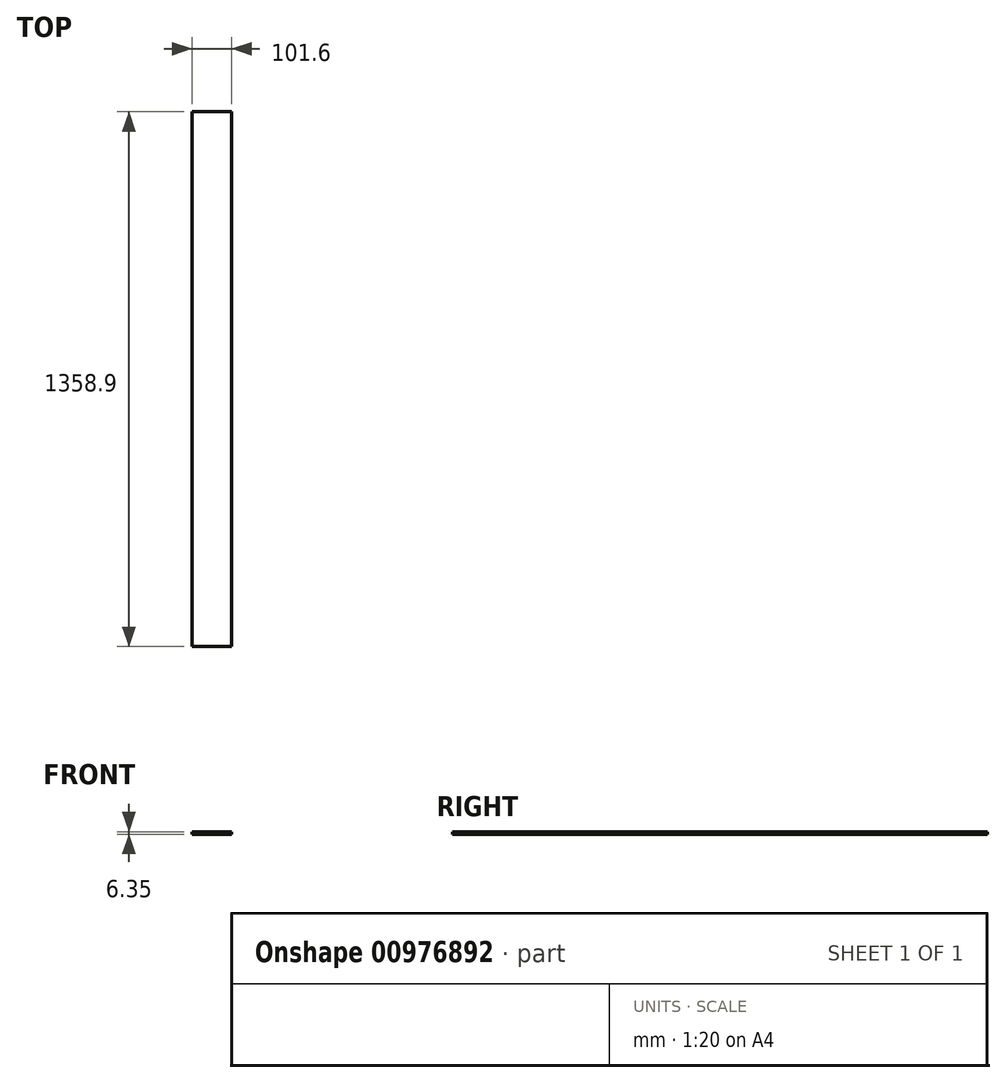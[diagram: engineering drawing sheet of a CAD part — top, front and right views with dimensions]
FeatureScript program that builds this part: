
annotation { "Feature Type Name" : "Feature", "Feature Type Description" : "" }
export const myFeature = defineFeature(function(context is Context, id is Id, definition is map)
    precondition{}
    {
        {
            var Q0;
            Q0=qCreatedBy(makeId("Front.planeOp"),FACE);
            var sketch = newSketch(context, id + "F0", { "sketchPlane" : qUnion([Q0])});
            skLineSegment(sketch, "E0.bottom", {"start": v(0, 0) * mm, "end": v(101.6, 0) * mm});
            skLineSegment(sketch, "E0.top", {"start": v(0, 6.35) * mm, "end": v(101.6, 6.35) * mm});
            skLineSegment(sketch, "E0.left", {"start": v(0, 0) * mm, "end": v(0, 6.35) * mm});
            skLineSegment(sketch, "E0.right", {"start": v(101.6, 0) * mm, "end": v(101.6, 6.35) * mm});
            skSolve(sketch);
        }
        {
            var Q0;
            Q0 = qSketchRegion(id + "F0", true);
            extrude(context, id + "F1", {"entities" : qUnion([Q0]), "oppositeDirection" : true, "depth" : 1358.9 * mm, "offsetDistance" : 25.4 * mm});
        }
    });
